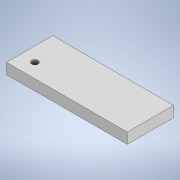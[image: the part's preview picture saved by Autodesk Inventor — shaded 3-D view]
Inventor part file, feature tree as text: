
AUTODESK INVENTOR PART (.ipt)
format: ipt  version: 2022 (Build 260153000, 153)  size: 97,280 bytes
history: native  units: mm
features: extrude x1, sketch x1
ambient origin geometry x8: Origin, YZ Plane, XZ Plane, XY Plane, X Axis, Y Axis, Z Axis, Center Point
bodies: Solid1 (feature_tree)
feature tree (2):
  extrude  "Extrusion1"  Depth=65.0mm
  sketch  "Sketch1"  dims[d0=170.0mm d1=65.0mm d2=20.0mm d3=20.0mm d4=9.0mm d5=15.0mm d6=0.0mm]
